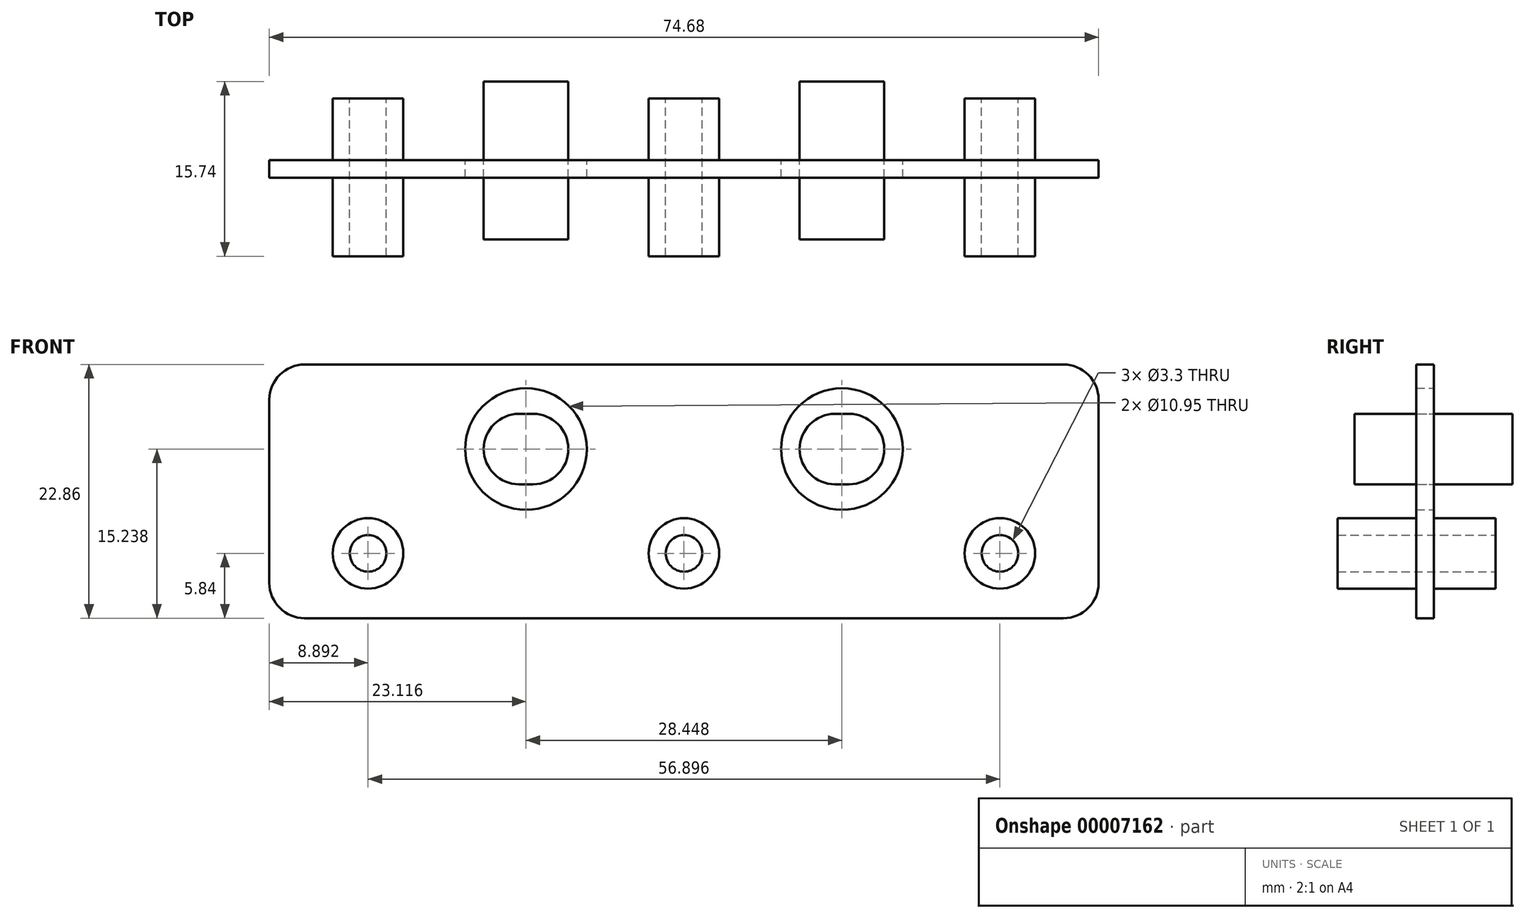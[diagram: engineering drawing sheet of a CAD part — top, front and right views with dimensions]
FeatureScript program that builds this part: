
annotation { "Feature Type Name" : "Feature", "Feature Type Description" : "" }
export const myFeature = defineFeature(function(context is Context, id is Id, definition is map)
    precondition{}
    {
        {
            var Q0;
            Q0=qCreatedBy(makeId("Front.planeOp"),FACE);
            var sketch = newSketch(context, id + "F0", { "sketchPlane" : qUnion([Q0])});
            skPoint(sketch, "E0", {"position": v(0, 0) * mm});
            skPoint(sketch, "E1", {"position": v(28.45, 0) * mm});
            skPoint(sketch, "E2", {"position": v(-28.45, 0) * mm});
            skCircle(sketch, "E3", {"center": v(-28.45, 0) * mm, "radius": 1.65 * mm});
            skCircle(sketch, "E4", {"center": v(0, 0) * mm, "radius": 1.65 * mm});
            skCircle(sketch, "E5", {"center": v(28.45, 0) * mm, "radius": 1.65 * mm});
            skCircle(sketch, "E6", {"center": v(-28.45, 0) * mm, "radius": 3.18 * mm});
            skCircle(sketch, "E7", {"center": v(0, 0) * mm, "radius": 3.18 * mm});
            skCircle(sketch, "E8", {"center": v(28.45, 0) * mm, "radius": 3.18 * mm});
            skLineSegment(sketch, "E9.bottom", {"start": v(-34.16, 17.02) * mm, "end": v(34.16, 17.02) * mm});
            skLineSegment(sketch, "E9.top", {"start": v(-34.16, -5.84) * mm, "end": v(34.16, -5.84) * mm});
            skLineSegment(sketch, "E9.left", {"start": v(-37.34, 13.84) * mm, "end": v(-37.34, -2.67) * mm});
            skLineSegment(sketch, "E9.right", {"start": v(37.34, 13.84) * mm, "end": v(37.34, -2.67) * mm});
            skLineSegment(sketch, "E10", {"start": v(-14.86, 9.4) * mm, "end": v(-13.59, 9.4) * mm});
            skLineSegment(sketch, "E11", {"start": v(13.59, 9.4) * mm, "end": v(14.86, 9.4) * mm});
            skPoint(sketch, "E12", {"position": v(-14.22, 9.4) * mm});
            skPoint(sketch, "E13", {"position": v(14.22, 9.4) * mm});
            skArc(sketch, "E14.0.startCap", {"start": v(-14.86, 6.22) * mm, "mid": v(-18.03, 9.4) * mm, "end": v(-14.86, 12.57) * mm});
            skArc(sketch, "E14.0.endCap", {"start": v(-13.59, 12.57) * mm, "mid": v(-10.41, 9.4) * mm, "end": v(-13.59, 6.22) * mm});
            skLineSegment(sketch, "E14.0.left", {"start": v(-14.86, 12.57) * mm, "end": v(-13.59, 12.57) * mm});
            skLineSegment(sketch, "E14.0.right", {"start": v(-14.86, 6.22) * mm, "end": v(-13.59, 6.22) * mm});
            skArc(sketch, "E15.0.startCap", {"start": v(13.59, 6.22) * mm, "mid": v(10.41, 9.4) * mm, "end": v(13.59, 12.57) * mm});
            skArc(sketch, "E15.0.endCap", {"start": v(14.86, 12.57) * mm, "mid": v(18.03, 9.4) * mm, "end": v(14.86, 6.22) * mm});
            skLineSegment(sketch, "E15.0.left", {"start": v(13.59, 12.57) * mm, "end": v(14.86, 12.57) * mm});
            skLineSegment(sketch, "E15.0.right", {"start": v(13.59, 6.22) * mm, "end": v(14.86, 6.22) * mm});
            skCircle(sketch, "E16", {"center": v(-14.22, 9.4) * mm, "radius": 5.48 * mm});
            skCircle(sketch, "E17", {"center": v(14.22, 9.4) * mm, "radius": 5.48 * mm});
            skPoint(sketch, "E18.visualSharp", {"position": v(-37.34, 17.02) * mm});
            skArc(sketch, "E18.filletArc", {"start": v(-34.16, 17.02) * mm, "mid": v(-36.4, 16.09) * mm, "end": v(-37.34, 13.84) * mm});
            skPoint(sketch, "E19.visualSharp", {"position": v(-37.34, -5.84) * mm});
            skArc(sketch, "E19.filletArc", {"start": v(-37.34, -2.67) * mm, "mid": v(-36.4, -4.91) * mm, "end": v(-34.16, -5.84) * mm});
            skPoint(sketch, "E20.visualSharp", {"position": v(37.34, 17.02) * mm});
            skArc(sketch, "E20.filletArc", {"start": v(37.34, 13.84) * mm, "mid": v(36.4, 16.09) * mm, "end": v(34.16, 17.02) * mm});
            skPoint(sketch, "E21.visualSharp", {"position": v(37.34, -5.84) * mm});
            skArc(sketch, "E21.filletArc", {"start": v(34.16, -5.84) * mm, "mid": v(36.4, -4.91) * mm, "end": v(37.34, -2.67) * mm});
            skSolve(sketch);
        }
        {
            var Q0;
            Q0=makeQuery(id+"F0.imprint","IMPRINT",FACE,{"disambiguationData":[TD([[makeQuery(id+"F0.imprint","IMPRINT",EDGE,{"derivedFrom":sQuery(id+"F0.wireOp",EDGE,"E6")}),-1.0]])]});
            var Q1;
            Q1=makeQuery(id+"F0.imprint","IMPRINT",FACE,{"disambiguationData":[TD([[makeQuery(id+"F0.imprint","IMPRINT",EDGE,{"derivedFrom":sQuery(id+"F0.wireOp",EDGE,"E14.0.startCap")}),1.0]])]});
            var Q2;
            Q2=makeQuery(id+"F0.imprint","IMPRINT",FACE,{"disambiguationData":[TD([[makeQuery(id+"F0.imprint","IMPRINT",EDGE,{"derivedFrom":sQuery(id+"F0.wireOp",EDGE,"E3")}),-1.0]])]});
            var Q3;
            Q3=makeQuery(id+"F0.imprint","IMPRINT",FACE,{"disambiguationData":[TD([[makeQuery(id+"F0.imprint","IMPRINT",EDGE,{"derivedFrom":sQuery(id+"F0.wireOp",EDGE,"E4")}),-1.0]])]});
            var Q4;
            Q4=makeQuery(id+"F0.imprint","IMPRINT",FACE,{"disambiguationData":[TD([[makeQuery(id+"F0.imprint","IMPRINT",EDGE,{"derivedFrom":sQuery(id+"F0.wireOp",EDGE,"E15.0.startCap")}),1.0]])]});
            var Q5;
            Q5=makeQuery(id+"F0.imprint","IMPRINT",FACE,{"disambiguationData":[TD([[makeQuery(id+"F0.imprint","IMPRINT",EDGE,{"derivedFrom":sQuery(id+"F0.wireOp",EDGE,"E5")}),-1.0]])]});
            extrude(context, id + "F1", {"entities" : qUnion([Q0, Q1, Q2, Q3, Q4, Q5]), "endBound" : BoundingType.SYMMETRIC, "depth" : 1.59 * mm});
        }
        {
            var Q0;
            Q0=makeQuery(id+"F0.imprint","IMPRINT",FACE,{"disambiguationData":[TD([[makeQuery(id+"F0.imprint","IMPRINT",EDGE,{"derivedFrom":sQuery(id+"F0.wireOp",EDGE,"E3")}),-1.0]])]});
            var Q1;
            Q1=makeQuery(id+"F0.imprint","IMPRINT",FACE,{"disambiguationData":[TD([[makeQuery(id+"F0.imprint","IMPRINT",EDGE,{"derivedFrom":sQuery(id+"F0.wireOp",EDGE,"E4")}),-1.0]])]});
            var Q2;
            Q2=makeQuery(id+"F0.imprint","IMPRINT",FACE,{"disambiguationData":[TD([[makeQuery(id+"F0.imprint","IMPRINT",EDGE,{"derivedFrom":sQuery(id+"F0.wireOp",EDGE,"E5")}),-1.0]])]});
            extrude(context, id + "F2", {"entities" : qUnion([Q0, Q1, Q2]), "operationType" : NewBodyOperationType.ADD, "depth" : 7.87 * mm, "hasSecondDirection" : true, "secondDirectionOppositeDirection" : true, "secondDirectionDepth" : 6.35 * mm});
        }
        {
            var Q0;
            Q0=makeQuery(id+"F0.imprint","IMPRINT",FACE,{"disambiguationData":[TD([[makeQuery(id+"F0.imprint","IMPRINT",EDGE,{"derivedFrom":sQuery(id+"F0.wireOp",EDGE,"E14.0.startCap")}),1.0]])]});
            var Q1;
            Q1=makeQuery(id+"F0.imprint","IMPRINT",FACE,{"disambiguationData":[TD([[makeQuery(id+"F0.imprint","IMPRINT",EDGE,{"derivedFrom":sQuery(id+"F0.wireOp",EDGE,"E15.0.startCap")}),1.0]])]});
            extrude(context, id + "F3", {"entities" : qUnion([Q0, Q1]), "operationType" : NewBodyOperationType.ADD, "depth" : 6.35 * mm, "hasSecondDirection" : true, "secondDirectionOppositeDirection" : true, "secondDirectionDepth" : 7.87 * mm});
        }
    });
